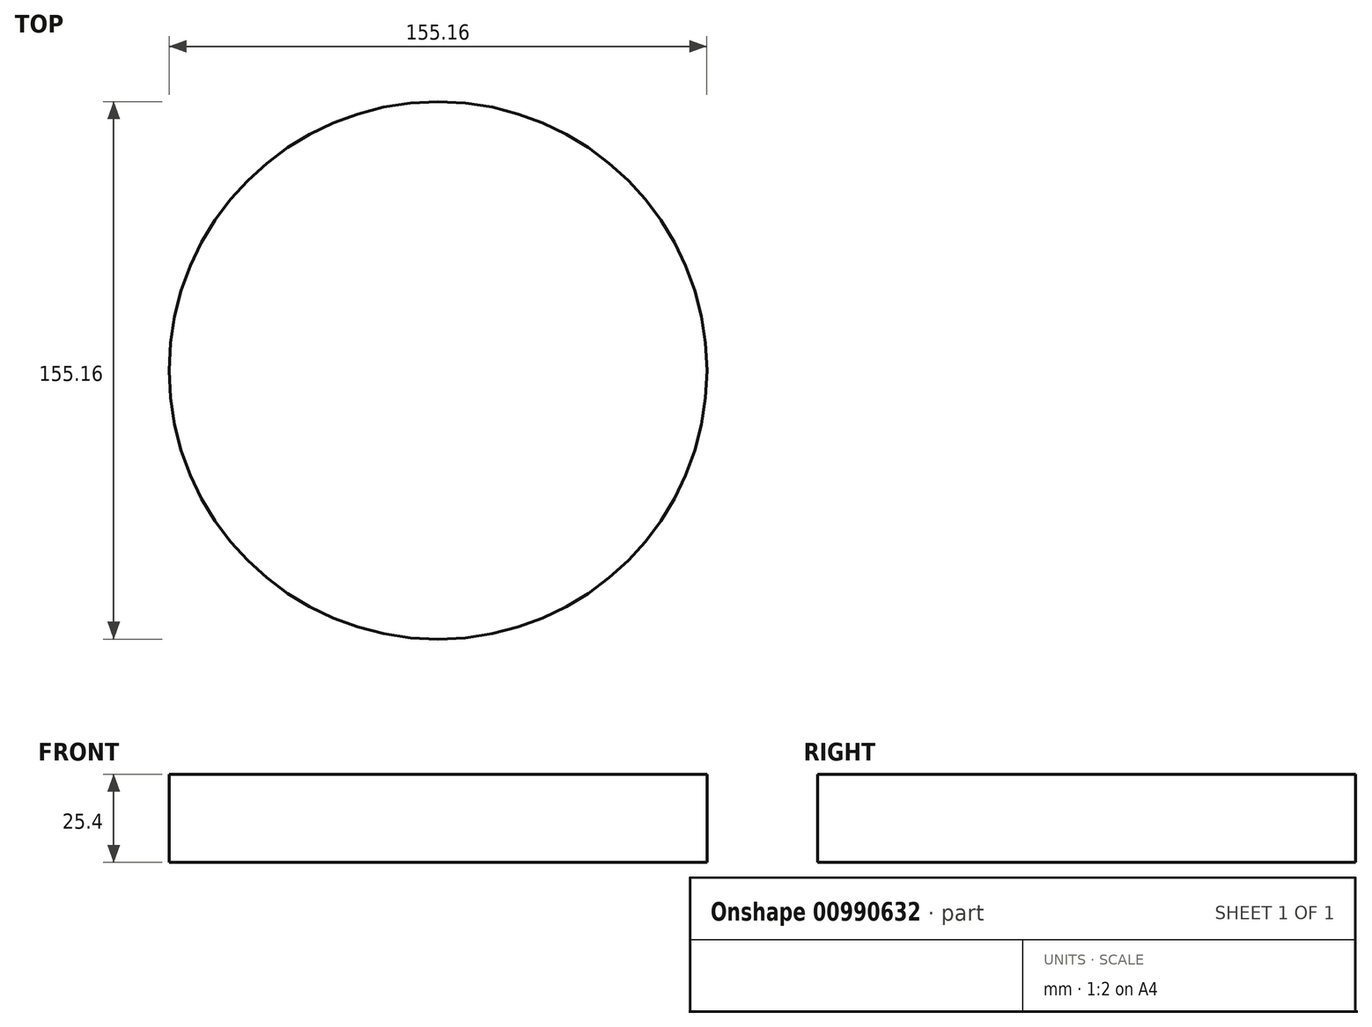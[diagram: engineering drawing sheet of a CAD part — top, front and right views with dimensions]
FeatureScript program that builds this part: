
annotation { "Feature Type Name" : "Feature", "Feature Type Description" : "" }
export const myFeature = defineFeature(function(context is Context, id is Id, definition is map)
    precondition{}
    {
        {
            var Q0;
            Q0=qCreatedBy(makeId("Top.planeOp"),FACE);
            var sketch = newSketch(context, id + "F0", { "sketchPlane" : qUnion([Q0])});
            skCircle(sketch, "E0", {"center": v(0, 0) * mm, "radius": 77.58 * mm});
            skSolve(sketch);
        }
        {
            var Q0;
            Q0 = qSketchRegion(id + "F0", true);
            extrude(context, id + "F1", {"entities" : qUnion([Q0]), "depth" : 25.4 * mm, "offsetDistance" : 25.4 * mm});
        }
    });
